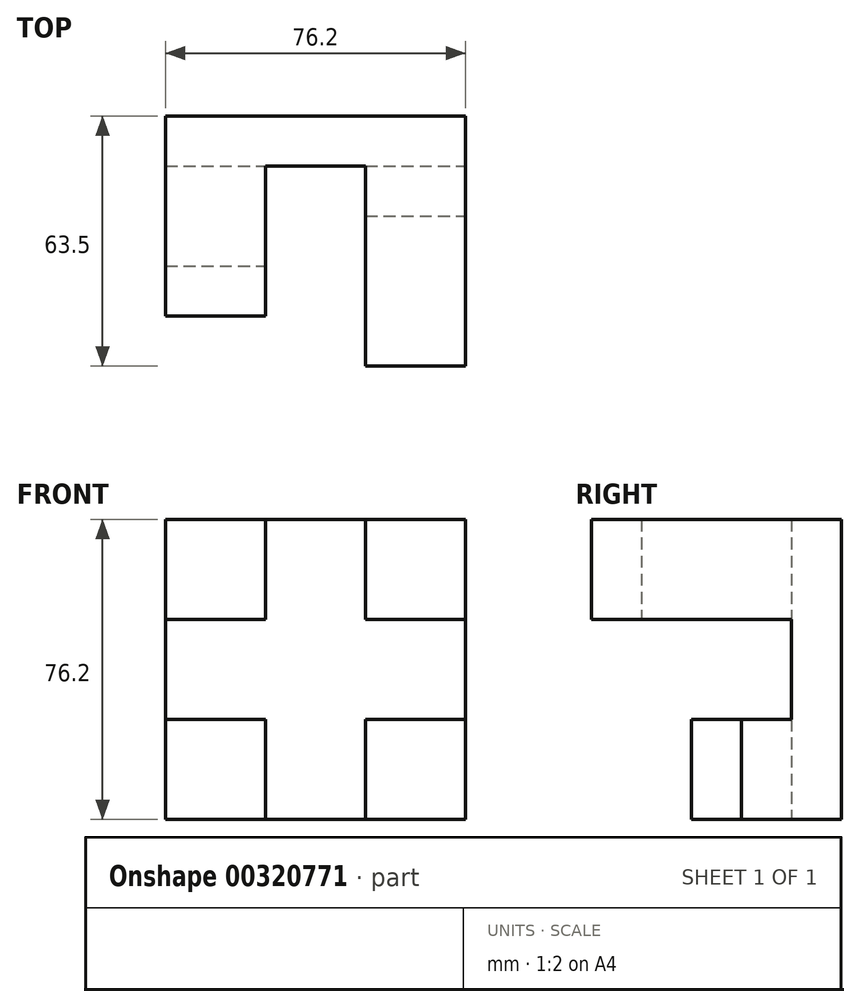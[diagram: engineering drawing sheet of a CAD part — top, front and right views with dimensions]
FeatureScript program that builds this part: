
annotation { "Feature Type Name" : "Feature", "Feature Type Description" : "" }
export const myFeature = defineFeature(function(context is Context, id is Id, definition is map)
    precondition{}
    {
        {
            var Q0;
            Q0=qCreatedBy(makeId("Front.planeOp"),FACE);
            var sketch = newSketch(context, id + "F0", { "sketchPlane" : qUnion([Q0])});
            skLineSegment(sketch, "E0", {"start": v(-42.28, -44.08) * mm, "end": v(33.92, -44.08) * mm});
            skLineSegment(sketch, "E1", {"start": v(33.92, -44.08) * mm, "end": v(33.92, 32.12) * mm});
            skLineSegment(sketch, "E2", {"start": v(33.92, 32.12) * mm, "end": v(-42.28, 32.12) * mm});
            skLineSegment(sketch, "E3", {"start": v(-42.28, 32.12) * mm, "end": v(-42.28, -44.08) * mm});
            skSolve(sketch);
        }
        {
            var Q0;
            Q0=makeQuery(id+"F0.imprint","IMPRINT",FACE,{"disambiguationData":[TD([[makeQuery(id+"F0.imprint","IMPRINT",EDGE,{"derivedFrom":sQuery(id+"F0.wireOp",EDGE,"E0")}),1.0]])]});
            extrude(context, id + "F1", {"entities" : qUnion([Q0]), "depth" : 12.7 * mm});
        }
        {
            var Q0;
            Q0=makeQuery(id+"F1.opExtrude","CAP_FACE",FACE,{"disambiguationData":[OSD([sQuery(id+"F0.wireOp",EDGE,"E0"),sQuery(id+"F0.wireOp",EDGE,"E1"),sQuery(id+"F0.wireOp",EDGE,"E2"),sQuery(id+"F0.wireOp",EDGE,"E3")])],"isStart":false});
            var sketch = newSketch(context, id + "F2", { "sketchPlane" : qUnion([Q0])});
            skLineSegment(sketch, "E4", {"start": v(8.52, -44.08) * mm, "end": v(8.52, -18.68) * mm});
            skLineSegment(sketch, "E5", {"start": v(8.52, -18.68) * mm, "end": v(33.92, -18.68) * mm});
            skLineSegment(sketch, "E6", {"start": v(8.52, 32.12) * mm, "end": v(8.52, 6.72) * mm});
            skLineSegment(sketch, "E7", {"start": v(8.52, 6.72) * mm, "end": v(33.92, 6.72) * mm});
            skLineSegment(sketch, "E8", {"start": v(-16.88, 32.12) * mm, "end": v(-16.88, 6.72) * mm});
            skLineSegment(sketch, "E9", {"start": v(-16.88, 6.72) * mm, "end": v(-42.28, 6.72) * mm});
            skLineSegment(sketch, "E10", {"start": v(-42.28, -18.68) * mm, "end": v(-16.88, -18.68) * mm});
            skLineSegment(sketch, "E11", {"start": v(-16.88, -18.68) * mm, "end": v(-16.88, -44.08) * mm});
            skSolve(sketch);
        }
        {
            var Q0;
            {var subQ0=sQuery(id+"F2.wireOp",EDGE,"E4");Q0=makeQuery(id+"F2.imprint","IMPRINT",FACE,{"disambiguationData":[TD([[makeQuery(id+"F2.imprint","IMPRINT",EDGE,{"derivedFrom":subQ0}),-1.0]])]});}
            extrude(context, id + "F3", {"entities" : qUnion([Q0]), "operationType" : NewBodyOperationType.ADD, "depth" : 12.7 * mm});
        }
        {
            var Q0;
            Q0=makeQuery(id+"F1.opExtrude","CAP_FACE",FACE,{"disambiguationData":[OSD([sQuery(id+"F0.wireOp",EDGE,"E0"),sQuery(id+"F0.wireOp",EDGE,"E1"),sQuery(id+"F0.wireOp",EDGE,"E2"),sQuery(id+"F0.wireOp",EDGE,"E3")])],"isStart":false});
            var sketch = newSketch(context, id + "F4", { "sketchPlane" : qUnion([Q0])});
            skLineSegment(sketch, "E12", {"start": v(-42.28, -18.68) * mm, "end": v(-16.88, -18.68) * mm});
            skLineSegment(sketch, "E13", {"start": v(-16.88, -18.68) * mm, "end": v(-16.88, -44.08) * mm});
            skSolve(sketch);
        }
        {
            var Q0;
            {var subQ0=sQuery(id+"F4.wireOp",EDGE,"E12");Q0=makeQuery(id+"F4.imprint","IMPRINT",FACE,{"disambiguationData":[TD([[makeQuery(id+"F4.imprint","IMPRINT",EDGE,{"derivedFrom":subQ0}),-1.0]])]});}
            extrude(context, id + "F5", {"entities" : qUnion([Q0]), "operationType" : NewBodyOperationType.ADD, "depth" : 25.4 * mm});
        }
        {
            var Q0;
            Q0=makeQuery(id+"F1.opExtrude","CAP_FACE",FACE,{"disambiguationData":[OSD([sQuery(id+"F0.wireOp",EDGE,"E0"),sQuery(id+"F0.wireOp",EDGE,"E1"),sQuery(id+"F0.wireOp",EDGE,"E2"),sQuery(id+"F0.wireOp",EDGE,"E3")])],"isStart":false});
            var sketch = newSketch(context, id + "F6", { "sketchPlane" : qUnion([Q0])});
            skLineSegment(sketch, "E14", {"start": v(-42.28, 6.72) * mm, "end": v(-16.88, 6.72) * mm});
            skLineSegment(sketch, "E15", {"start": v(-16.88, 6.72) * mm, "end": v(-16.88, 32.12) * mm});
            skSolve(sketch);
        }
        {
            var Q0;
            {var subQ0=sQuery(id+"F6.wireOp",EDGE,"E14");Q0=makeQuery(id+"F6.imprint","IMPRINT",FACE,{"disambiguationData":[TD([[makeQuery(id+"F6.imprint","IMPRINT",EDGE,{"derivedFrom":subQ0}),1.0]])]});}
            extrude(context, id + "F7", {"entities" : qUnion([Q0]), "operationType" : NewBodyOperationType.ADD, "depth" : 38.1 * mm});
        }
        {
            var Q0;
            Q0=makeQuery(id+"F1.opExtrude","CAP_FACE",FACE,{"disambiguationData":[OSD([sQuery(id+"F0.wireOp",EDGE,"E0"),sQuery(id+"F0.wireOp",EDGE,"E1"),sQuery(id+"F0.wireOp",EDGE,"E2"),sQuery(id+"F0.wireOp",EDGE,"E3")])],"isStart":false});
            var sketch = newSketch(context, id + "F8", { "sketchPlane" : qUnion([Q0])});
            skLineSegment(sketch, "E16", {"start": v(8.52, 32.12) * mm, "end": v(8.52, 6.72) * mm});
            skLineSegment(sketch, "E17", {"start": v(8.52, 6.72) * mm, "end": v(33.92, 6.72) * mm});
            skSolve(sketch);
        }
        {
            var Q0;
            {var subQ0=sQuery(id+"F8.wireOp",EDGE,"E16");Q0=makeQuery(id+"F8.imprint","IMPRINT",FACE,{"disambiguationData":[TD([[makeQuery(id+"F8.imprint","IMPRINT",EDGE,{"derivedFrom":subQ0}),1.0]])]});}
            extrude(context, id + "F9", {"entities" : qUnion([Q0]), "operationType" : NewBodyOperationType.ADD, "depth" : 50.8 * mm});
        }
    });
